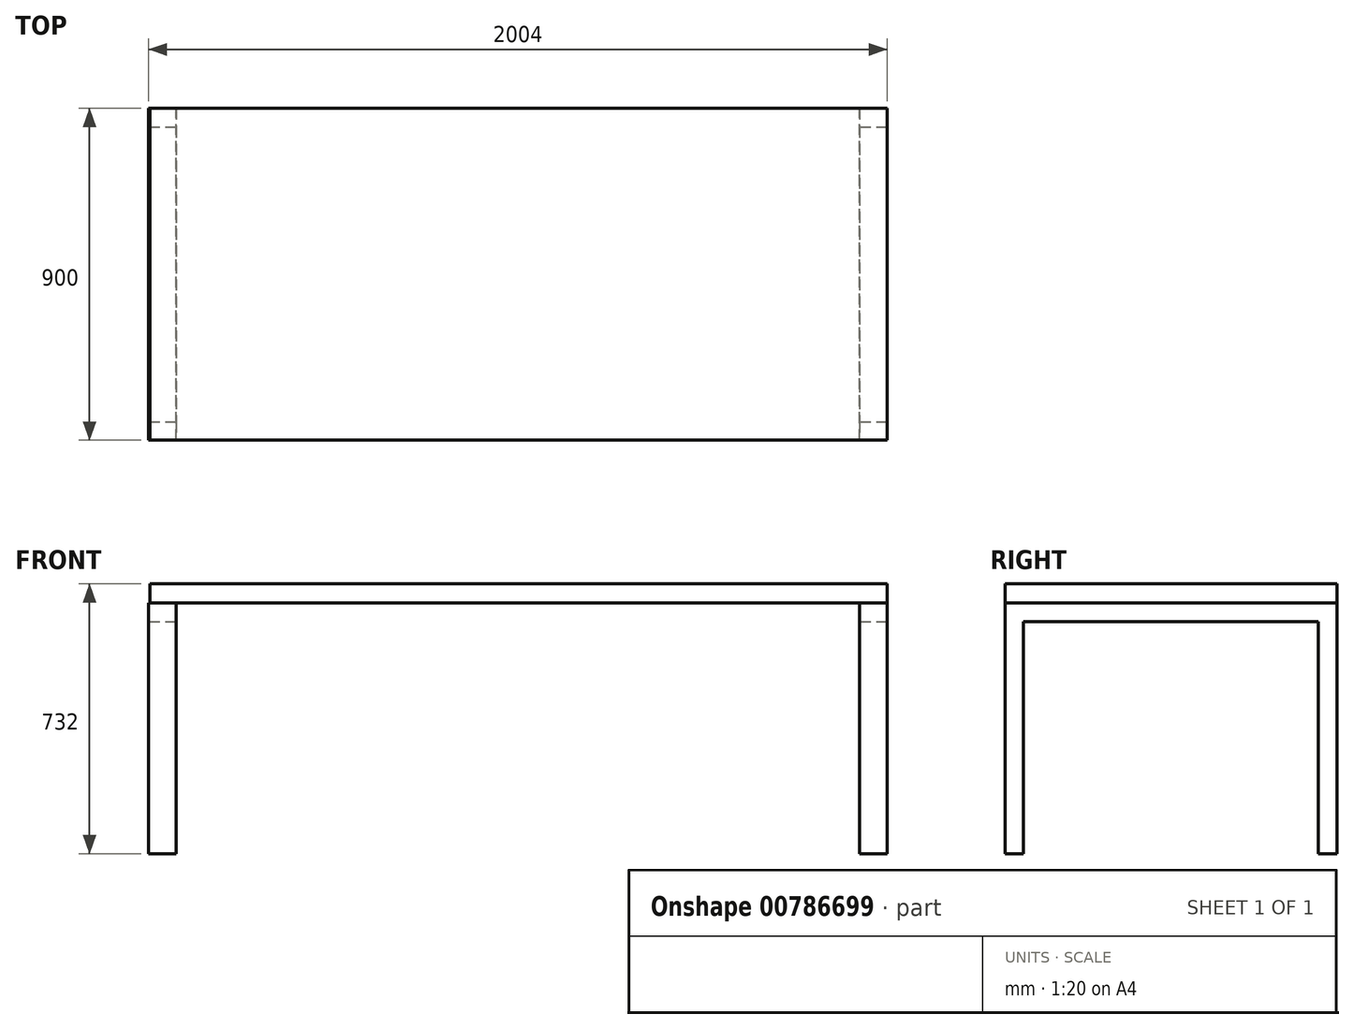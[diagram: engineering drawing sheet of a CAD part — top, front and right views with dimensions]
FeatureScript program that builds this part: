
annotation { "Feature Type Name" : "Feature", "Feature Type Description" : "" }
export const myFeature = defineFeature(function(context is Context, id is Id, definition is map)
    precondition{}
    {
        {
            var Q0;
            Q0=qCreatedBy(makeId("Top.planeOp"),FACE);
            var sketch = newSketch(context, id + "F0", { "sketchPlane" : qUnion([Q0])});
            skLineSegment(sketch, "E0.bottom", {"start": v(0, 0) * mm, "end": v(2000, 0) * mm});
            skLineSegment(sketch, "E0.top", {"start": v(0, 900) * mm, "end": v(2000, 900) * mm});
            skLineSegment(sketch, "E0.left", {"start": v(0, 0) * mm, "end": v(0, 900) * mm});
            skLineSegment(sketch, "E0.right", {"start": v(2000, 0) * mm, "end": v(2000, 900) * mm});
            skSolve(sketch);
        }
        {
            var Q0;
            Q0=makeQuery(id+"F0.imprint","IMPRINT",FACE,{"disambiguationData":[TD([[makeQuery(id+"F0.imprint","IMPRINT",EDGE,{"derivedFrom":sQuery(id+"F0.wireOp",EDGE,"E0.bottom")}),1.0]])]});
            extrude(context, id + "F1", {"entities" : qUnion([Q0]), "depth" : 52 * mm, "offsetDistance" : 25 * mm});
        }
        {
            var Q0;
            Q0=makeQuery(id+"F1.opExtrude","SWEPT_FACE",FACE,{"disambiguationData":[OSD([sQuery(id+"F0.wireOp",EDGE,"E0.right")])]});
            var sketch = newSketch(context, id + "F2", { "sketchPlane" : qUnion([Q0])});
            skLineSegment(sketch, "E1", {"start": v(0, -680) * mm, "end": v(0, 0) * mm});
            skLineSegment(sketch, "E2", {"start": v(0, 0) * mm, "end": v(900, 0) * mm});
            skLineSegment(sketch, "E3", {"start": v(900, 0) * mm, "end": v(900, -680) * mm});
            skLineSegment(sketch, "E4", {"start": v(900, -680) * mm, "end": v(850, -680) * mm});
            skLineSegment(sketch, "E5", {"start": v(850, -680) * mm, "end": v(850, -50) * mm});
            skLineSegment(sketch, "E6", {"start": v(850, -50) * mm, "end": v(50, -50) * mm});
            skLineSegment(sketch, "E7", {"start": v(50, -50) * mm, "end": v(50, -680) * mm});
            skLineSegment(sketch, "E8", {"start": v(50, -680) * mm, "end": v(0, -680) * mm});
            skSolve(sketch);
        }
        {
            var Q0;
            Q0=makeQuery(id+"F2.imprint","IMPRINT",FACE,{"disambiguationData":[TD([[makeQuery(id+"F2.imprint","IMPRINT",EDGE,{"derivedFrom":sQuery(id+"F2.wireOp",EDGE,"E1")}),-1.0]])]});
            extrude(context, id + "F3", {"entities" : qUnion([Q0]), "oppositeDirection" : true, "depth" : 75 * mm, "offsetDistance" : 25 * mm});
        }
        {
            var Q0;
            Q0=makeQuery(id+"F3.opExtrude","SWEPT_BODY",BODY,{"disambiguationData":[OSD([sQuery(id+"F2.wireOp",EDGE,"E1"),sQuery(id+"F2.wireOp",EDGE,"E2"),sQuery(id+"F2.wireOp",EDGE,"E3"),sQuery(id+"F2.wireOp",EDGE,"E4"),sQuery(id+"F2.wireOp",EDGE,"E5"),sQuery(id+"F2.wireOp",EDGE,"E6"),sQuery(id+"F2.wireOp",EDGE,"E7"),sQuery(id+"F2.wireOp",EDGE,"E8")])]});
            transform(context, id + "F4", {"entities" : qUnion([Q0]), "transformType" : TransformType.TRANSLATION_3D, "dx" : -1929 * mm, "dy" : 0 * mm, "dz" : 0 * mm, "makeCopy" : true});
        }
    });
